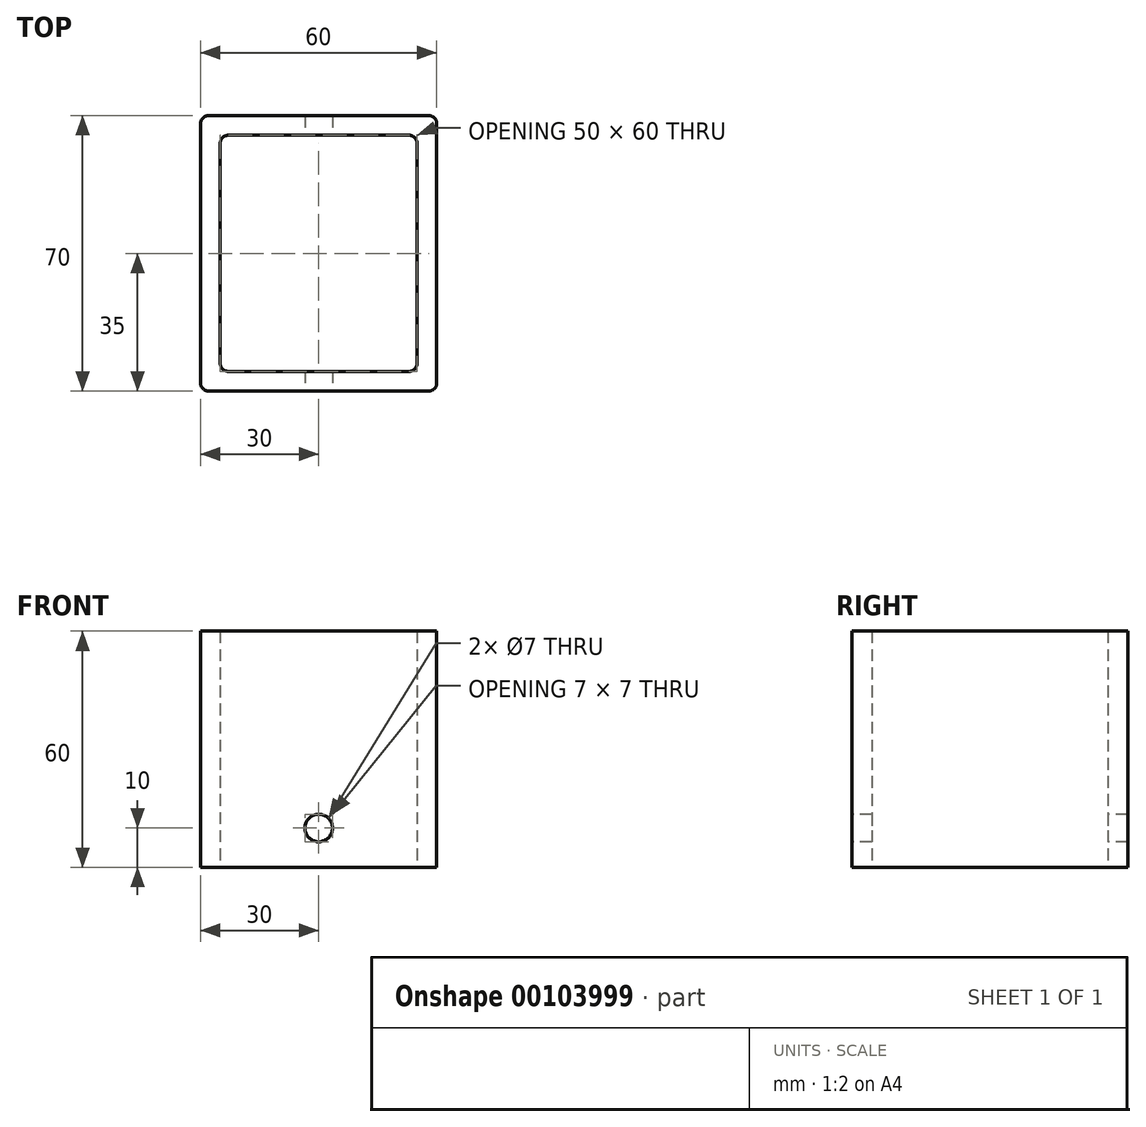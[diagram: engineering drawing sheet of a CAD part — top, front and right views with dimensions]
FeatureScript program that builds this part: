
annotation { "Feature Type Name" : "Feature", "Feature Type Description" : "" }
export const myFeature = defineFeature(function(context is Context, id is Id, definition is map)
    precondition{}
    {
        {
            var Q0;
            Q0=qCreatedBy(makeId("Top.planeOp"),FACE);
            var sketch = newSketch(context, id + "F0", { "sketchPlane" : qUnion([Q0])});
            skLineSegment(sketch, "E0.bottom", {"start": v(-25, 30) * mm, "end": v(25, 30) * mm});
            skLineSegment(sketch, "E0.top", {"start": v(-25, -30) * mm, "end": v(25, -30) * mm});
            skLineSegment(sketch, "E0.left", {"start": v(-25, 30) * mm, "end": v(-25, -30) * mm});
            skLineSegment(sketch, "E0.right", {"start": v(25, 30) * mm, "end": v(25, -30) * mm});
            skPoint(sketch, "E0.middle", {"position": v(0, 0) * mm});
            skLineSegment(sketch, "E1.bottom", {"start": v(-30, 35) * mm, "end": v(30, 35) * mm});
            skLineSegment(sketch, "E1.top", {"start": v(-30, -35) * mm, "end": v(30, -35) * mm});
            skLineSegment(sketch, "E1.left", {"start": v(-30, 35) * mm, "end": v(-30, -35) * mm});
            skLineSegment(sketch, "E1.right", {"start": v(30, 35) * mm, "end": v(30, -35) * mm});
            skSolve(sketch);
        }
        {
            var Q0;
            Q0=makeQuery(id+"F0.imprint","IMPRINT",FACE,{"disambiguationData":[TD([[makeQuery(id+"F0.imprint","IMPRINT",EDGE,{"derivedFrom":sQuery(id+"F0.wireOp",EDGE,"E0.bottom")}),1.0]])]});
            extrude(context, id + "F1", {"entities" : qUnion([Q0]), "depth" : 60 * mm});
        }
        {
            var Q0;
            Q0=makeQuery(id+"F1.opExtrude","SWEPT_EDGE",EDGE,{"disambiguationData":[OSD([sQuery(id+"F0.wireOp",EDGE,"E1.bottom"),sQuery(id+"F0.wireOp",EDGE,"E1.left")])]});
            var Q1;
            Q1=makeQuery(id+"F1.opExtrude","SWEPT_EDGE",EDGE,{"disambiguationData":[OSD([sQuery(id+"F0.wireOp",EDGE,"E1.bottom"),sQuery(id+"F0.wireOp",EDGE,"E1.right")])]});
            var Q2;
            Q2=makeQuery(id+"F1.opExtrude","SWEPT_EDGE",EDGE,{"disambiguationData":[OSD([sQuery(id+"F0.wireOp",EDGE,"E1.top"),sQuery(id+"F0.wireOp",EDGE,"E1.right")])]});
            var Q3;
            Q3=makeQuery(id+"F1.opExtrude","SWEPT_EDGE",EDGE,{"disambiguationData":[OSD([sQuery(id+"F0.wireOp",EDGE,"E1.top"),sQuery(id+"F0.wireOp",EDGE,"E1.left")])]});
            var Q4;
            Q4=makeQuery(id+"F1.opExtrude","SWEPT_EDGE",EDGE,{"disambiguationData":[OSD([sQuery(id+"F0.wireOp",EDGE,"E0.bottom"),sQuery(id+"F0.wireOp",EDGE,"E0.left")])]});
            var Q5;
            Q5=makeQuery(id+"F1.opExtrude","SWEPT_EDGE",EDGE,{"disambiguationData":[OSD([sQuery(id+"F0.wireOp",EDGE,"E0.top"),sQuery(id+"F0.wireOp",EDGE,"E0.left")])]});
            var Q6;
            Q6=makeQuery(id+"F1.opExtrude","SWEPT_EDGE",EDGE,{"disambiguationData":[OSD([sQuery(id+"F0.wireOp",EDGE,"E0.top"),sQuery(id+"F0.wireOp",EDGE,"E0.right")])]});
            var Q7;
            Q7=makeQuery(id+"F1.opExtrude","SWEPT_EDGE",EDGE,{"disambiguationData":[OSD([sQuery(id+"F0.wireOp",EDGE,"E0.bottom"),sQuery(id+"F0.wireOp",EDGE,"E0.right")])]});
            fillet(context, id + "F2", {"entities" : qUnion([Q0, Q1, Q2, Q3, Q4, Q5, Q6, Q7]), "radius" : 2 * mm, "tangentPropagation" : true, "allowEdgeOverflow" : false});
        }
        {
            var Q0;
            Q0=makeQuery(id+"F1.opExtrude","SWEPT_FACE",FACE,{"disambiguationData":[OSD([sQuery(id+"F0.wireOp",EDGE,"E1.top")])]});
            var sketch = newSketch(context, id + "F3", { "sketchPlane" : qUnion([Q0])});
            skCircle(sketch, "E2", {"center": v(0, 10) * mm, "radius": 3.5 * mm});
            skSolve(sketch);
        }
        {
            var Q0;
            Q0=makeQuery(id+"F3.imprint","IMPRINT",FACE,{"disambiguationData":[TD([[makeQuery(id+"F3.imprint","IMPRINT",EDGE,{"derivedFrom":sQuery(id+"F3.wireOp",EDGE,"E2")}),1.0]])]});
            extrude(context, id + "F4", {"entities" : qUnion([Q0]), "operationType" : NewBodyOperationType.REMOVE, "oppositeDirection" : true, "depth" : 70 * mm});
        }
    });
